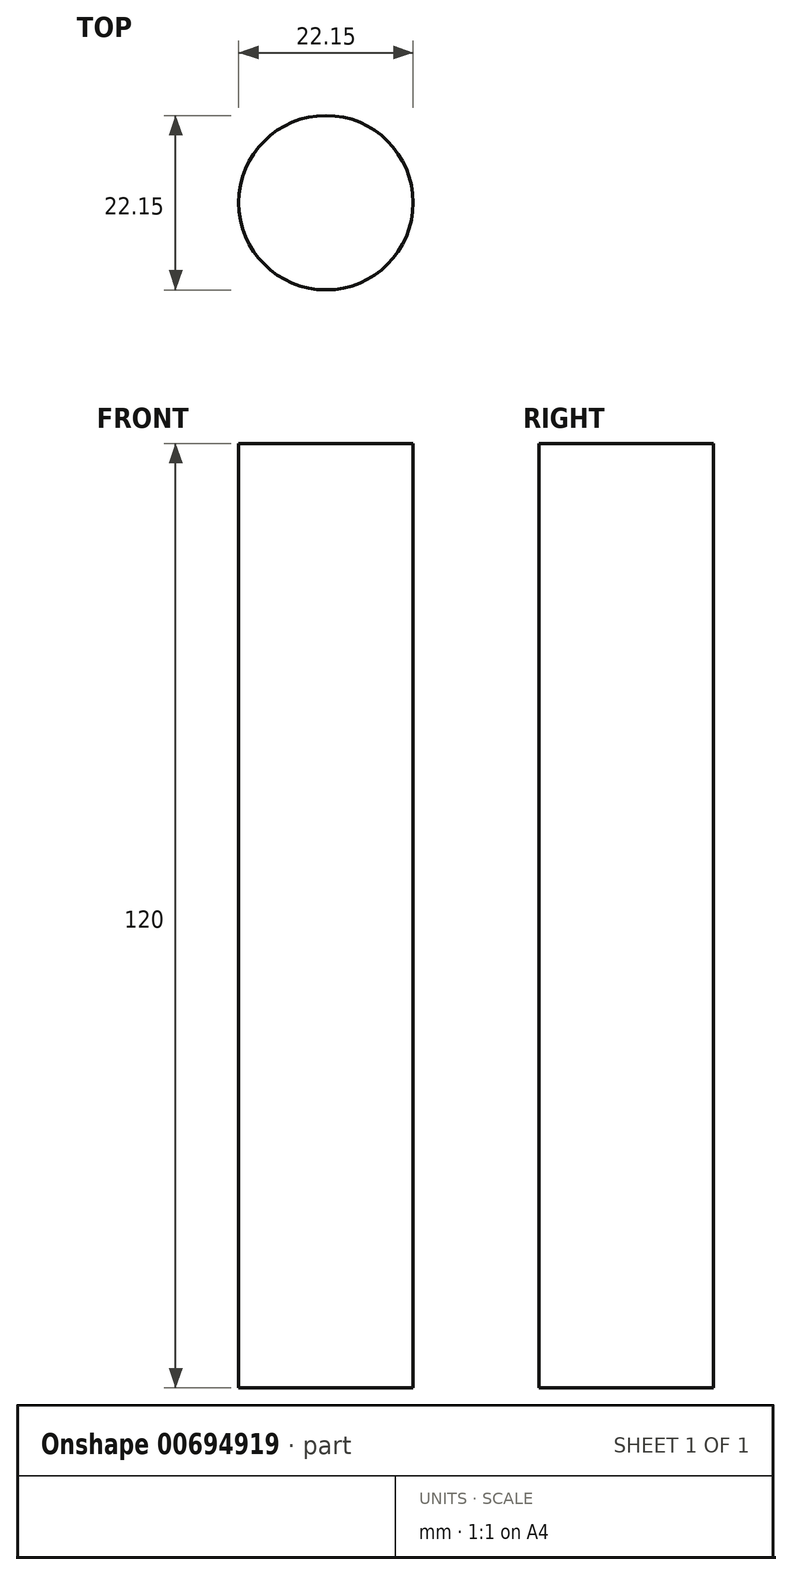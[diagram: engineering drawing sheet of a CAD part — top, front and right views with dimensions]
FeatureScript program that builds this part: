
annotation { "Feature Type Name" : "Feature", "Feature Type Description" : "" }
export const myFeature = defineFeature(function(context is Context, id is Id, definition is map)
    precondition{}
    {
        {
            var Q0;
            Q0=qCreatedBy(makeId("Top.planeOp"),FACE);
            var sketch = newSketch(context, id + "F0", { "sketchPlane" : qUnion([Q0])});
            skCircle(sketch, "E0", {"center": v(61.38, 61.25) * mm, "radius": 11.08 * mm});
            skSolve(sketch);
        }
        {
            var Q0;
            Q0=sQuery(id+"F0.wireOp",EDGE,"E0");
            extrude(context, id + "F1", {"bodyType" : ToolBodyType.SURFACE, "surfaceEntities" : qUnion([Q0]), "depth" : 120 * mm, "offsetDistance" : 25 * mm});
        }
    });
